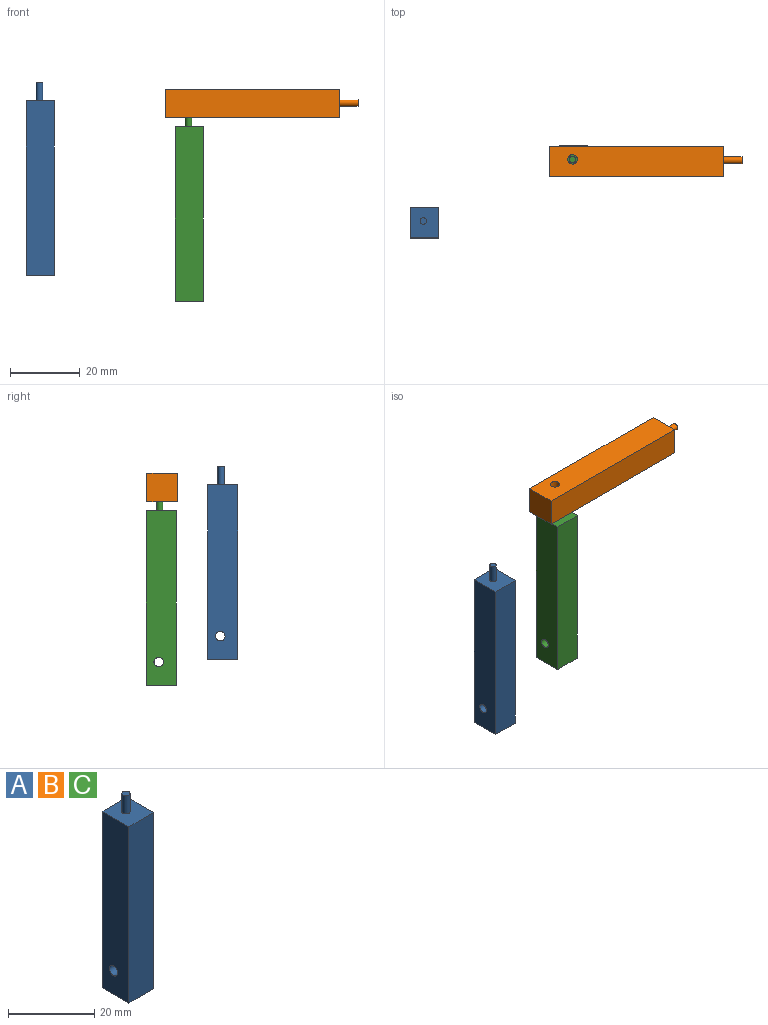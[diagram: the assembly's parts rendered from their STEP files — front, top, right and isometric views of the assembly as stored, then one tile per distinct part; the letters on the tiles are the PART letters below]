
ASSEMBLY  parts=3 mates=1
PART A: 9 faces, bbox 8.1x8.7x55.3 mm
  f0: plane 50.1x8.66mm, normal (-1,0,0), area 427.9mm2, adj f1,f3,f4,f5,f6
  f1: plane 50.1x8.11mm, normal (0,-1,0), area 406.5mm2, adj f0,f2,f4,f5
  f2: plane 50.1x8.66mm, normal (1,0,0), area 427.9mm2, adj f1,f3,f4,f5,f6
  f3: plane 50.1x8.11mm, normal (0,1,0), area 406.5mm2, adj f0,f2,f4,f5
  f4: plane 8.66x8.11mm, normal (0,0,1), area 67.4mm2, adj f0,f1,f2,f3,f7
  f5: plane 8.66x8.11mm, normal (0,0,-1), area 70.2mm2, adj f0,f1,f2,f3
  f6: cylinder r=1.35mm len=8.11mm, axis (1,0,0), area 69mm2, adj f0,f2
  f7: cylinder r=0.95mm len=5.2mm, axis (0,0,-1), area 30.9mm2, adj f4,f8
  f8: plane 1.89x1.89mm, normal (0,0,1), area 2.8mm2, adj f7
PART B: same geometry as A
PART C: same geometry as A
PLACE A t=(-26.2,8.15,-2.74)mm
PLACE B rot(axis=(0,1,0),90deg) t=(13.8,25.59,50.65)mm
PLACE C t=(16.62,25.84,-10.17)mm
MATE revolute B.f6 <-> C.f7  axis (0,0,-1) through (20.46,21.98,42.53)mm
